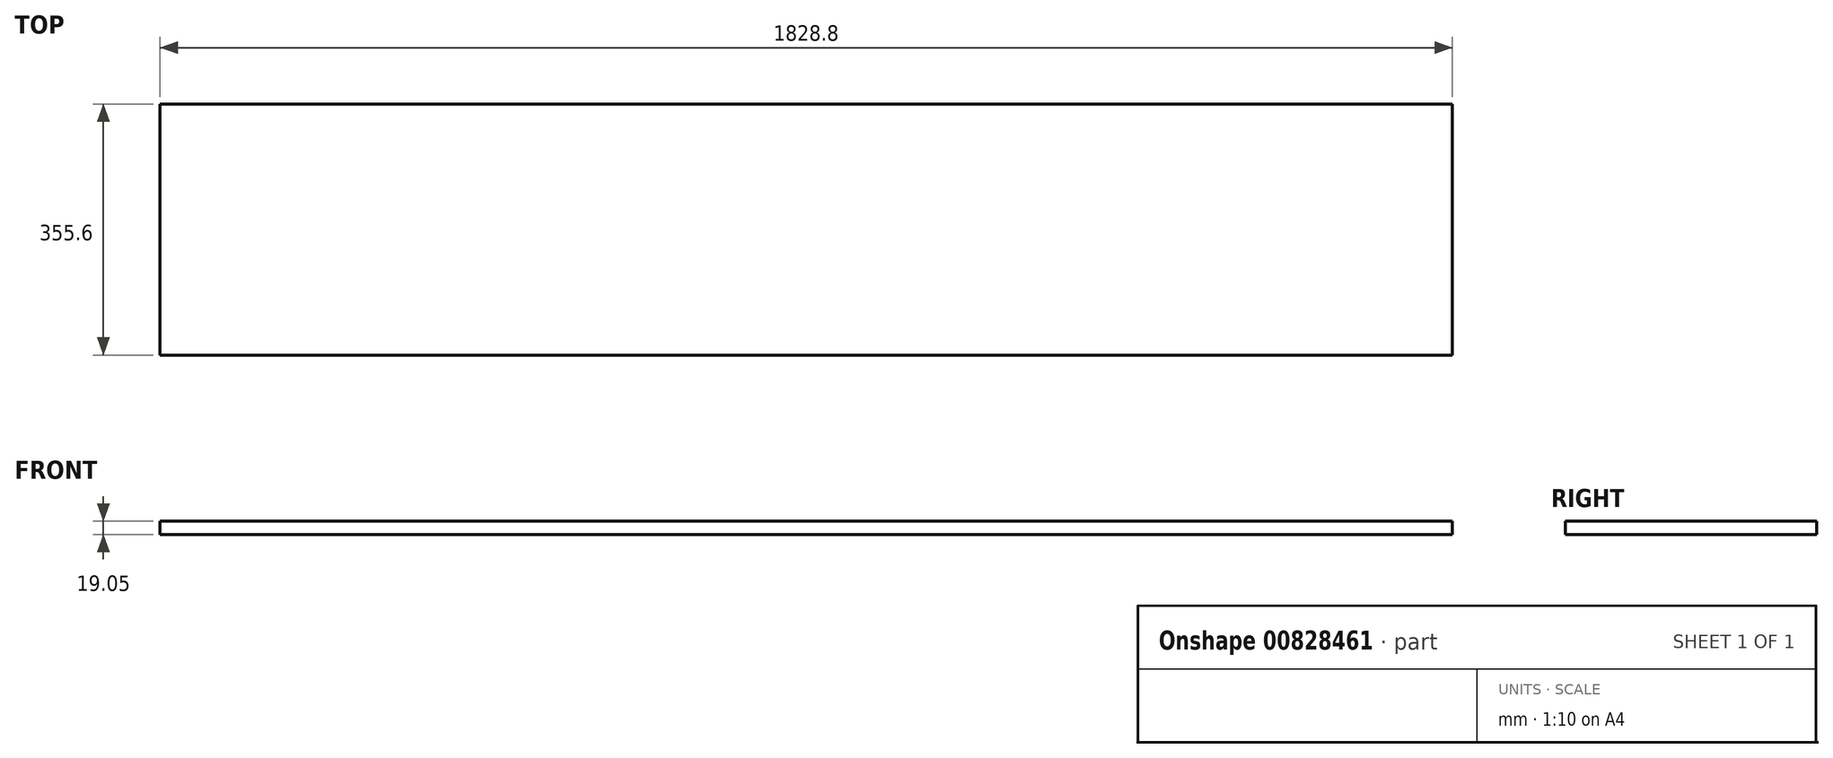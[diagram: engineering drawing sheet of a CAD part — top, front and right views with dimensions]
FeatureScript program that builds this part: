
annotation { "Feature Type Name" : "Feature", "Feature Type Description" : "" }
export const myFeature = defineFeature(function(context is Context, id is Id, definition is map)
    precondition{}
    {
        {
            var Q0;
            Q0=qCreatedBy(makeId("Top.planeOp"),FACE);
            var sketch = newSketch(context, id + "F0", { "sketchPlane" : qUnion([Q0])});
            skLineSegment(sketch, "E0.bottom", {"start": v(914.4, 177.8) * mm, "end": v(-914.4, 177.8) * mm});
            skLineSegment(sketch, "E0.top", {"start": v(914.4, -177.8) * mm, "end": v(-914.4, -177.8) * mm});
            skLineSegment(sketch, "E0.left", {"start": v(914.4, 177.8) * mm, "end": v(914.4, -177.8) * mm});
            skLineSegment(sketch, "E0.right", {"start": v(-914.4, 177.8) * mm, "end": v(-914.4, -177.8) * mm});
            skPoint(sketch, "E0.middle", {"position": v(0, 0) * mm});
            skSolve(sketch);
        }
        {
            var Q0;
            Q0=makeQuery(id+"F0.imprint","IMPRINT",FACE,{"disambiguationData":[TD([[makeQuery(id+"F0.imprint","IMPRINT",EDGE,{"derivedFrom":sQuery(id+"F0.wireOp",EDGE,"E0.bottom")}),1.0]])]});
            extrude(context, id + "F1", {"entities" : qUnion([Q0]), "depth" : 19.05 * mm, "offsetDistance" : 25.4 * mm});
        }
    });
